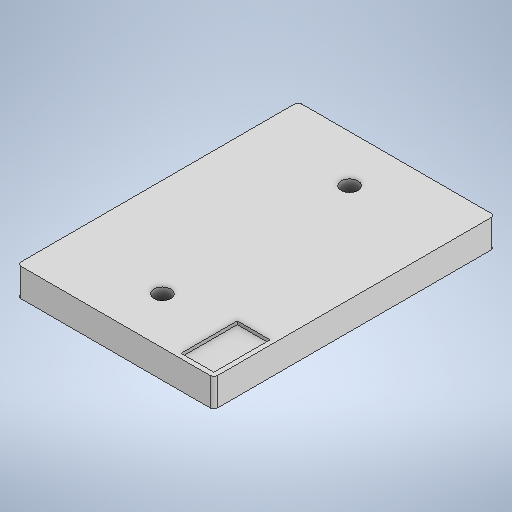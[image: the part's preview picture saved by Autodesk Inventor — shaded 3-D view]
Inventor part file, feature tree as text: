
AUTODESK INVENTOR PART (.ipt)
format: ipt  version: 2025 (Build 290162000, 162)  size: 241,664 bytes
history: native  units: in
note: dims shown in document units (in); Inventor stores cm internally (conversion verified against a paired STEP export)
features: sketch x3, extrude x2, hole x1, fillet x1
ambient origin geometry x8: Origin, YZ Plane, XZ Plane, XY Plane, X Axis, Y Axis, Z Axis, Center Point
bodies: Solid1 (feature_tree)
feature tree (7):
  extrude  "Extrusion1"  Depth=11.811in
  hole  "Hole1"  [1 undecoded]
  extrude  "Extrusion2"  Depth=0.1575in
  fillet  "Fillet1"  Radius=3.937in
  sketch  "Sketch1"  dims[d0=8.2677in d1=11.811in]
  sketch  "Sketch2"  dims[d2=1.1811in d3=0.0in d4=0.7087in]
  sketch  "Sketch3"  dims[d5=0.7087in d6=3.937in d7=3.937in d8=0.0039in d9=0.2341in d10=0.7087in d11=0.9449in d12=90.0deg d13=0.315in d14=0.8108in d15=1.378in d16=2.3622in d17=0.1969in d19=0.1969in d20=0.1378in d21=0.0in d22=0.1575in]
note: 1 required parameter value undecoded (feature->parameter linkage not recoverable at this tier; creation-order binding heuristic only, values carry confidence <= 0.55)
